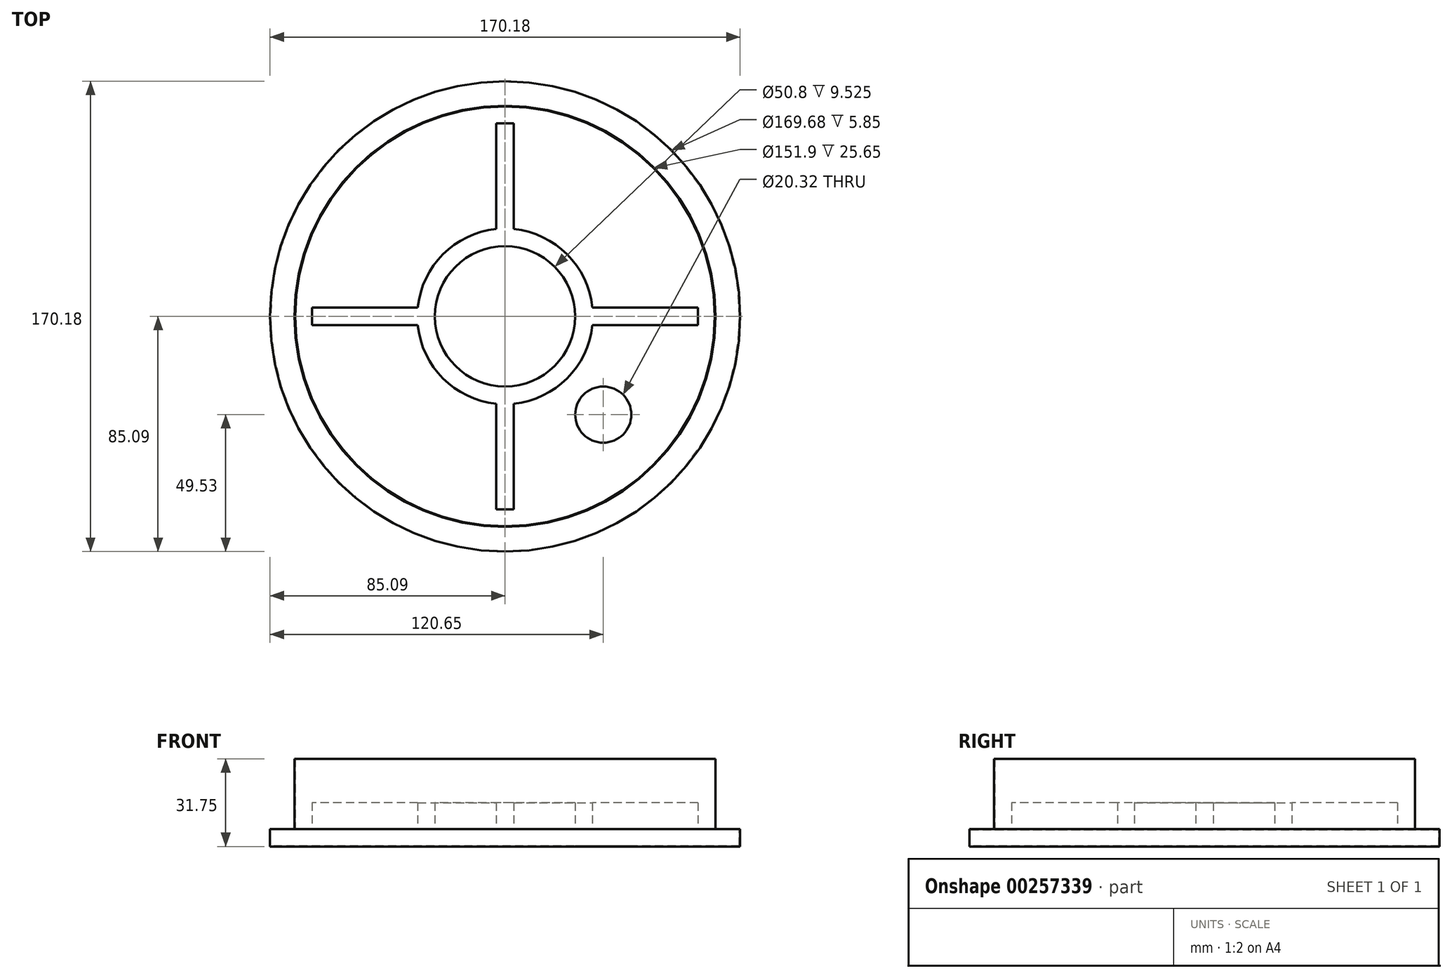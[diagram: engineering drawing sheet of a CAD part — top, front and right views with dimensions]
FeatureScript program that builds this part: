
annotation { "Feature Type Name" : "Feature", "Feature Type Description" : "" }
export const myFeature = defineFeature(function(context is Context, id is Id, definition is map)
    precondition{}
    {
        {
            assignVariable(context, id + "F0", {"name" : "thk", "anyValue" : .250});
        }
        {
            var Q0;
            Q0=qCreatedBy(makeId("Top.planeOp"),FACE);
            var sketch = newSketch(context, id + "F1", { "sketchPlane" : qUnion([Q0])});
            skCircle(sketch, "E0", {"center": v(0, 0) * mm, "radius": 85.1 * mm});
            skCircle(sketch, "E1", {"center": v(0, 0) * mm, "radius": 76.2 * mm});
            skSolve(sketch);
        }
        {
            var Q0;
            Q0=makeQuery(id+"F1.imprint","IMPRINT",FACE,{"disambiguationData":[TD([[makeQuery(id+"F1.imprint","IMPRINT",EDGE,{"derivedFrom":sQuery(id+"F1.wireOp",EDGE,"E0")}),1.0]])]});
            var Q1;
            Q1=makeQuery(id+"F1.imprint","IMPRINT",FACE,{"disambiguationData":[TD([[makeQuery(id+"F1.imprint","IMPRINT",EDGE,{"derivedFrom":sQuery(id+"F1.wireOp",EDGE,"E1")}),1.0]])]});
            extrude(context, id + "F2", {"entities" : qUnion([Q0, Q1]), "oppositeDirection" : true, "depth" : 6.35 * mm});
        }
        {
            var Q0;
            Q0=makeQuery(id+"F1.imprint","IMPRINT",FACE,{"disambiguationData":[TD([[makeQuery(id+"F1.imprint","IMPRINT",EDGE,{"derivedFrom":sQuery(id+"F1.wireOp",EDGE,"E1")}),1.0]])]});
            extrude(context, id + "F3", {"entities" : qUnion([Q0]), "operationType" : NewBodyOperationType.ADD, "depth" : 25.4 * mm});
        }
        {
            var Q0;
            Q0=makeQuery(id+"F3.opExtrude","CAP_FACE",FACE,{"disambiguationData":[OSD([sQuery(id+"F1.wireOp",EDGE,"E1")])],"isStart":false});
            shell(context, id + "F4", {"entities" : qUnion([Q0]), "thickness" : (getVariable(context, 'thk')) * mm});
        }
        {
            var Q0;
            Q0=makeQuery(id+"F1.imprint","IMPRINT",FACE,{"disambiguationData":[TD([[makeQuery(id+"F1.imprint","IMPRINT",EDGE,{"derivedFrom":sQuery(id+"F1.wireOp",EDGE,"E1")}),1.0]])]});
            var sketch = newSketch(context, id + "F5", { "sketchPlane" : qUnion([Q0])});
            skLineSegment(sketch, "E2.bottom", {"start": v(69.85, 3.18) * mm, "end": v(31.6, 3.18) * mm});
            skLineSegment(sketch, "E2.top", {"start": v(69.85, -3.17) * mm, "end": v(31.6, -3.17) * mm});
            skLineSegment(sketch, "E2.left", {"start": v(69.85, 3.18) * mm, "end": v(69.85, -3.18) * mm});
            skLineSegment(sketch, "E2.right", {"start": v(-69.85, 3.18) * mm, "end": v(-69.85, -3.18) * mm});
            skPoint(sketch, "E2.middle", {"position": v(0, 0) * mm});
            skLineSegment(sketch, "E3.bottom", {"start": v(3.18, 69.85) * mm, "end": v(-3.18, 69.85) * mm});
            skLineSegment(sketch, "E3.top", {"start": v(3.18, -69.85) * mm, "end": v(-3.18, -69.85) * mm});
            skLineSegment(sketch, "E3.left", {"start": v(3.18, 69.85) * mm, "end": v(3.18, 31.6) * mm});
            skLineSegment(sketch, "E3.right", {"start": v(-3.18, 69.85) * mm, "end": v(-3.18, 31.6) * mm});
            skCircle(sketch, "E4", {"center": v(0, 0) * mm, "radius": 25.4 * mm});
            skArc(sketch, "E5.0", {"start": v(-3.18, 31.6) * mm, "mid": v(-22.45, 22.45) * mm, "end": v(-31.6, 3.18) * mm});
            skLineSegment(sketch, "E6.trimOffspring", {"start": v(-31.6, 3.18) * mm, "end": v(-69.85, 3.18) * mm});
            skArc(sketch, "E7.trimOffspring", {"start": v(-31.6, -3.18) * mm, "mid": v(-22.45, -22.45) * mm, "end": v(-3.18, -31.6) * mm});
            skLineSegment(sketch, "E8.trimOffspring", {"start": v(-31.6, -3.18) * mm, "end": v(-69.85, -3.18) * mm});
            skLineSegment(sketch, "E9.trimOffspring", {"start": v(-3.18, -31.6) * mm, "end": v(-3.18, -69.85) * mm});
            skArc(sketch, "E10.trimOffspring", {"start": v(3.18, -31.6) * mm, "mid": v(22.45, -22.45) * mm, "end": v(31.6, -3.17) * mm});
            skLineSegment(sketch, "E11.trimOffspring", {"start": v(3.18, -31.6) * mm, "end": v(3.18, -69.85) * mm});
            skArc(sketch, "E12.trimOffspring", {"start": v(31.6, 3.17) * mm, "mid": v(22.45, 22.45) * mm, "end": v(3.18, 31.6) * mm});
            skSolve(sketch);
        }
        {
            var Q0;
            Q0=makeQuery(id+"F5.imprint","IMPRINT",FACE,{"disambiguationData":[TD([[makeQuery(id+"F5.imprint","IMPRINT",EDGE,{"derivedFrom":sQuery(id+"F5.wireOp",EDGE,"E2.bottom")}),1.0]])]});
            extrude(context, id + "F6", {"entities" : qUnion([Q0]), "operationType" : NewBodyOperationType.ADD, "depth" : 9.52 * mm});
        }
        {
            var Q0;
            Q0=makeQuery(id+"F1.imprint","IMPRINT",FACE,{"disambiguationData":[TD([[makeQuery(id+"F1.imprint","IMPRINT",EDGE,{"derivedFrom":sQuery(id+"F1.wireOp",EDGE,"E1")}),1.0]])]});
            var sketch = newSketch(context, id + "F7", { "sketchPlane" : qUnion([Q0])});
            skCircle(sketch, "E13", {"center": v(35.56, -35.56) * mm, "radius": 10.16 * mm});
            skSolve(sketch);
        }
        {
            var Q0;
            Q0=makeQuery(id+"F7.imprint","IMPRINT",FACE,{"disambiguationData":[TD([[makeQuery(id+"F7.imprint","IMPRINT",EDGE,{"derivedFrom":sQuery(id+"F7.wireOp",EDGE,"E13")}),1.0]])]});
            extrude(context, id + "F8", {"entities" : qUnion([Q0]), "operationType" : NewBodyOperationType.REMOVE, "oppositeDirection" : true, "depth" : 25.4 * mm});
        }
    });
